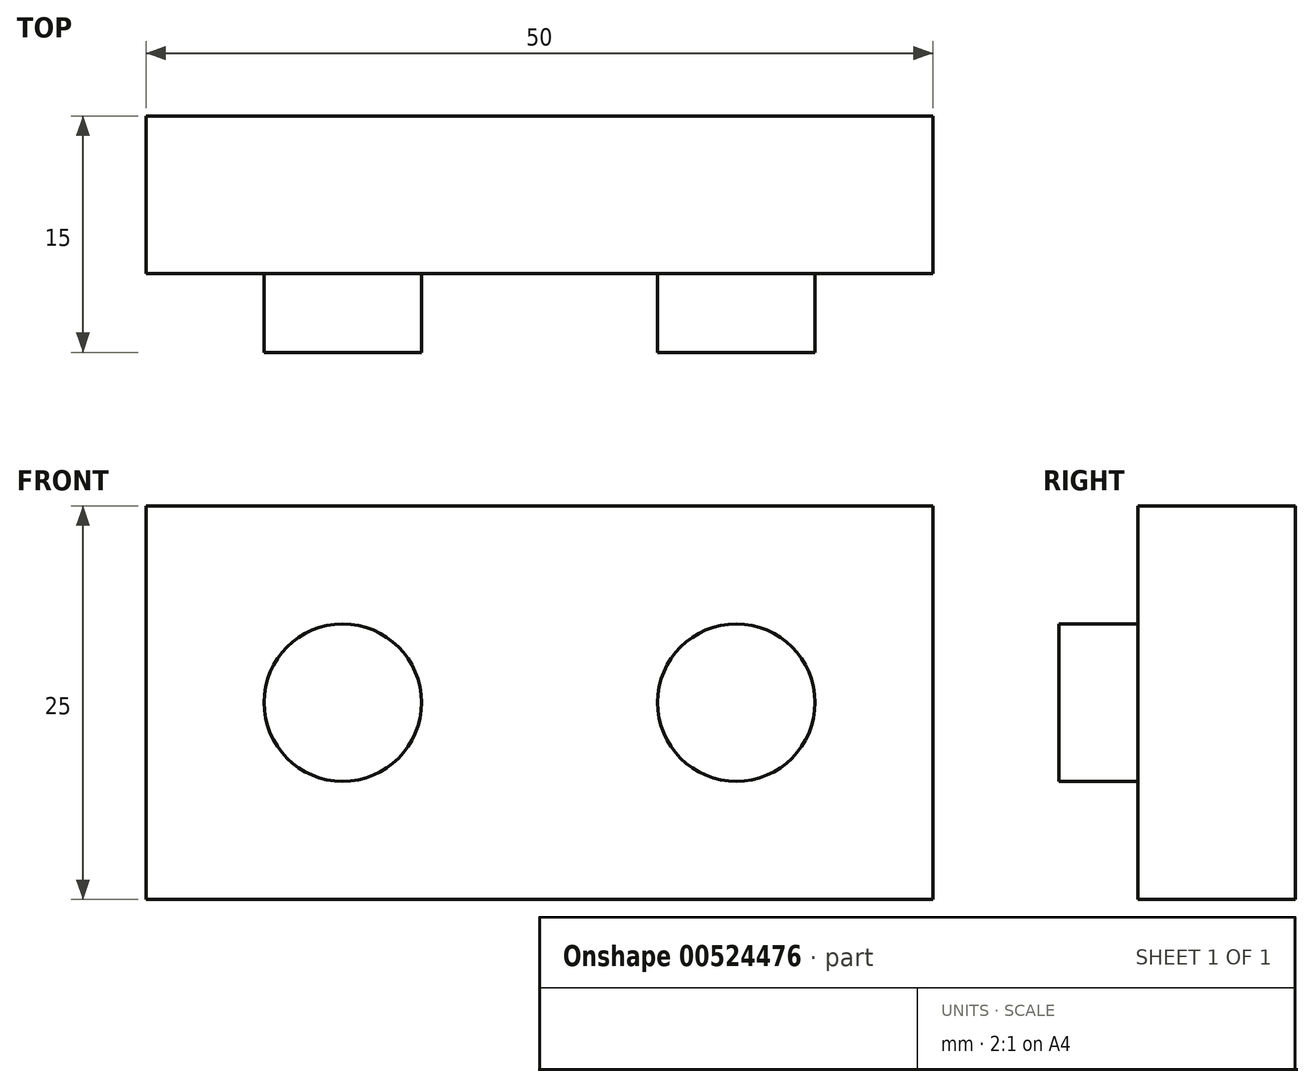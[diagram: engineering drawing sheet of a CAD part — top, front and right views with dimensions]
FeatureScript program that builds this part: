
annotation { "Feature Type Name" : "Feature", "Feature Type Description" : "" }
export const myFeature = defineFeature(function(context is Context, id is Id, definition is map)
    precondition{}
    {
        {
            var Q0;
            Q0=qCreatedBy(makeId("Front.planeOp"),FACE);
            var sketch = newSketch(context, id + "F0", { "sketchPlane" : qUnion([Q0])});
            skLineSegment(sketch, "E0.bottom", {"start": v(25, 12.5) * mm, "end": v(-25, 12.5) * mm});
            skLineSegment(sketch, "E0.top", {"start": v(25, -12.5) * mm, "end": v(-25, -12.5) * mm});
            skLineSegment(sketch, "E0.left", {"start": v(25, 12.5) * mm, "end": v(25, -12.5) * mm});
            skLineSegment(sketch, "E0.right", {"start": v(-25, 12.5) * mm, "end": v(-25, -12.5) * mm});
            skPoint(sketch, "E0.middle", {"position": v(0, 0) * mm});
            skSolve(sketch);
        }
        {
            var Q0;
            Q0 = qSketchRegion(id + "F0", true);
            extrude(context, id + "F1", {"entities" : qUnion([Q0]), "depth" : 10 * mm, "offsetDistance" : 25 * mm});
        }
        {
            var Q0;
            Q0=makeQuery(id+"F1.opExtrude","CAP_FACE",FACE,{"disambiguationData":[OSD([sQuery(id+"F0.wireOp",EDGE,"E0.bottom"),sQuery(id+"F0.wireOp",EDGE,"E0.top"),sQuery(id+"F0.wireOp",EDGE,"E0.left"),sQuery(id+"F0.wireOp",EDGE,"E0.right")])],"isStart":false});
            var sketch = newSketch(context, id + "F2", { "sketchPlane" : qUnion([Q0])});
            skLineSegment(sketch, "E1", {"start": v(0, 0) * mm, "end": v(25, 0) * mm, "construction": true});
            skLineSegment(sketch, "E2", {"start": v(12.5, 0) * mm, "end": v(12.5, -12.5) * mm, "construction": true});
            skLineSegment(sketch, "E3", {"start": v(0, 0) * mm, "end": v(-25, 0) * mm, "construction": true});
            skLineSegment(sketch, "E4", {"start": v(-12.5, 0) * mm, "end": v(-12.5, -12.5) * mm, "construction": true});
            skCircle(sketch, "E5", {"center": v(12.5, 0) * mm, "radius": 5 * mm});
            skCircle(sketch, "E6", {"center": v(-12.5, 0) * mm, "radius": 5 * mm});
            skSolve(sketch);
        }
        {
            var Q0;
            Q0 = qSketchRegion(id + "F2", true);
            extrude(context, id + "F3", {"entities" : qUnion([Q0]), "operationType" : NewBodyOperationType.ADD, "depth" : 5 * mm, "offsetDistance" : 25 * mm});
        }
    });
